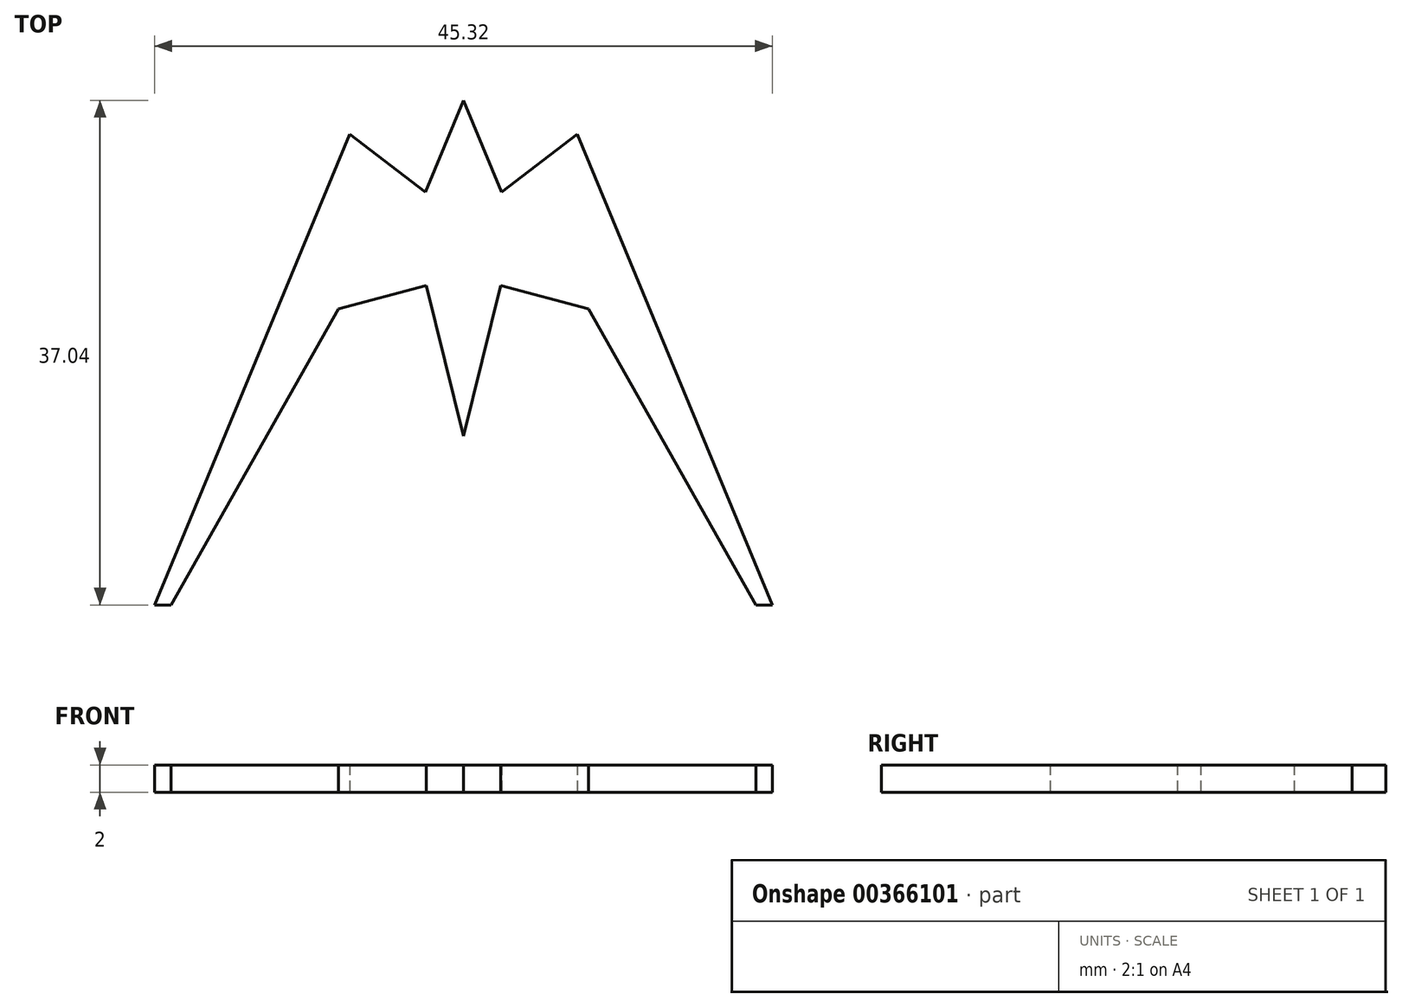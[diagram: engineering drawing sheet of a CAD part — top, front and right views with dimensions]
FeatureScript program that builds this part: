
annotation { "Feature Type Name" : "Feature", "Feature Type Description" : "" }
export const myFeature = defineFeature(function(context is Context, id is Id, definition is map)
    precondition{}
    {
        {
            var Q0;
            Q0=qCreatedBy(makeId("Top.planeOp"),FACE);
            var sketch = newSketch(context, id + "F0", { "sketchPlane" : qUnion([Q0])});
            skLineSegment(sketch, "E0", {"start": v(0, 14.35) * mm, "end": v(2.87, 7.42) * mm});
            skLineSegment(sketch, "E1", {"start": v(2.87, 7.42) * mm, "end": v(8.42, 11.68) * mm});
            skLineSegment(sketch, "E2", {"start": v(8.42, 11.68) * mm, "end": v(22.96, -23.41) * mm});
            skLineSegment(sketch, "E3", {"start": v(22.96, -23.41) * mm, "end": v(21.36, -23.41) * mm});
            skLineSegment(sketch, "E4", {"start": v(21.36, -23.41) * mm, "end": v(9.05, -1.65) * mm});
            skLineSegment(sketch, "E5", {"start": v(9.05, -1.65) * mm, "end": v(2.87, 0) * mm});
            skLineSegment(sketch, "E6", {"start": v(2.87, 0) * mm, "end": v(0, -11.65) * mm});
            skLineSegment(sketch, "E7", {"start": v(0, 14.35) * mm, "end": v(0, -11.65) * mm, "construction": true});
            skLineSegment(sketch, "E8.MirrorCS", {"start": v(0, 14.35) * mm, "end": v(-2.87, 7.42) * mm});
            skLineSegment(sketch, "E9.MirrorCS", {"start": v(-2.87, 7.42) * mm, "end": v(-8.42, 11.68) * mm});
            skLineSegment(sketch, "E10.MirrorCS", {"start": v(-8.42, 11.68) * mm, "end": v(-22.96, -23.41) * mm});
            skLineSegment(sketch, "E11.MirrorCS", {"start": v(-2.87, 0) * mm, "end": v(0, -11.65) * mm});
            skLineSegment(sketch, "E12.MirrorCS", {"start": v(-9.05, -1.65) * mm, "end": v(-2.87, 0) * mm});
            skLineSegment(sketch, "E13.MirrorCS", {"start": v(-21.36, -23.41) * mm, "end": v(-9.05, -1.65) * mm});
            skLineSegment(sketch, "E14.MirrorCS", {"start": v(-22.96, -23.41) * mm, "end": v(-21.36, -23.41) * mm});
            skLineSegment(sketch, "E15.0", {"start": v(0, 13.83) * mm, "end": v(-2.79, 7.1) * mm});
            skLineSegment(sketch, "E15.1", {"start": v(-2.79, 7.1) * mm, "end": v(-8.34, 11.36) * mm});
            skLineSegment(sketch, "E15.2", {"start": v(-8.34, 11.36) * mm, "end": v(-22.66, -23.21) * mm});
            skLineSegment(sketch, "E15.3", {"start": v(21.48, -23.21) * mm, "end": v(9.18, -1.48) * mm});
            skLineSegment(sketch, "E15.4", {"start": v(22.66, -23.21) * mm, "end": v(21.48, -23.21) * mm});
            skLineSegment(sketch, "E15.5", {"start": v(8.34, 11.36) * mm, "end": v(22.66, -23.21) * mm});
            skLineSegment(sketch, "E15.6", {"start": v(2.79, 7.1) * mm, "end": v(8.34, 11.36) * mm});
            skLineSegment(sketch, "E15.7", {"start": v(9.18, -1.48) * mm, "end": v(2.72, 0.25) * mm});
            skLineSegment(sketch, "E15.8", {"start": v(2.72, 0.25) * mm, "end": v(0, -10.82) * mm});
            skLineSegment(sketch, "E15.9", {"start": v(-2.72, 0.25) * mm, "end": v(0, -10.82) * mm});
            skLineSegment(sketch, "E15.10", {"start": v(0, 13.83) * mm, "end": v(2.79, 7.1) * mm});
            skLineSegment(sketch, "E15.11", {"start": v(-9.18, -1.48) * mm, "end": v(-2.72, 0.25) * mm});
            skLineSegment(sketch, "E15.12", {"start": v(-21.48, -23.21) * mm, "end": v(-9.18, -1.48) * mm});
            skLineSegment(sketch, "E15.13", {"start": v(-22.66, -23.21) * mm, "end": v(-21.48, -23.21) * mm});
            skSolve(sketch);
        }
        {
            var Q0;
            Q0=makeQuery(id+"F0.imprint","IMPRINT",FACE,{"disambiguationData":[TD([[makeQuery(id+"F0.imprint","IMPRINT",EDGE,{"derivedFrom":sQuery(id+"F0.wireOp",EDGE,"E15.0")}),1.0]])]});
            extrude(context, id + "F1", {"entities" : qUnion([Q0]), "depth" : 2 * mm});
        }
    });
